# Revit family: Pipefitting_IBP_Conex_MaxiPro_ReducingStraightCoupler_MP5240
name_source: partatom
category: Pipe Fittings
units: mm (PartAtom-declared; Revit-internal decimal feet)

## family parameters
Always vertical = No
Cut with Voids When Loaded = No
OmniClass Number = 23.65.00.00
OmniClass Title = Supply and Distribution of Liquids and Gases
Part Type = Transition
Round Connector Dimension = Use Diameter
Shared = No
Work Plane-Based = No

## types (15) — shared parameters
Angle = 30.00°
Application = Air conditioning & refrigeration
Assembly Code = D20
AssetType = Fixed
BIMObjectName = PipefittingP_IBP_Conex_MaxiPro_ReducingStraightcoupler_MP5240
ClassificationName = Uniclass2015
ClassificationValue = Pr_65_52_63_18
Description = Reducing Straight Coupler
ExpectedServiceLifeYears = 25
FittingType = Reducing Straight Coupler
FluidTemperatureMax = 121 °C
FluidTemperatureMin = -40 °C
IfcExportAs = IfcPipeFitting
IfcExportType = IfcPipeFittingType
Keynote = S
Manufacturer = Conex Banninger
ManufacturerName = IBP
Material = Copper, C12200
MaterialType = Refrigerant Grade Copper, C12200
MaxHydrostaticPressure = 48 bar
NBSDescription = Copper pipeline fittings
NBSObjectName = IBP - Copper pipeline fittings
NBSReference = 90-10-65/315
ORingTemperatureRange = -40°C to 140°C
PipeConnectorType = Press x Press
PressJawCompatability = MaxiPro Jaws supplied by Rothenberger
SealType = HNBR
Shape = Cylindrical
SurfaceFinish = Natural
URL = http://www.conexbanninger.com
WarrantyDescription = Product Guarantee
WarrantyDurationMonths = 60
Weight = 0.00 kg
_BimstoreBibleVersion = 14
_CurrentRevision = 1
_DistributedBy = www.bimmepaus.com.au/
zero-valued in all types: NominalDepth, NominalHeight, NominalLength, _BimSpecGuid

## per-type parameters (varying)
| type | A_OverallLength | Bead_Dia | Bead_Dia1 | DN | DN1 | L2_BeadLocation_Left | L2_BeadLocation_Right | L2_BeadLocation_Right_Formula | Length | Model | ModelNumber | ModelReference | OD | OD1 | ProductCode | Size | TubeStop | TubeStop1 | TubeStop1_Formula | Type Comments |
| MP5240 0030200 3/8" x 1/4" | 44 mm  [stored 0.144357 ft] | 2 mm  [stored 0.00656168 ft] | 2 mm  [stored 0.00656168 ft] | 10 mm  [stored 0.0328084 ft] | 6 mm  [stored 0.019685 ft] | 7 mm  [stored 0.0229659 ft] | 8 mm  [stored 0.0262467 ft] | 37 mm | 44 mm  [stored 0.144357 ft] | MP5240 0030200 | MP5240 0030200 | 3/8" x 1/2" | 12 mm  [stored 0.0393701 ft] | 8 mm  [stored 0.0262467 ft] | MP5240 0030200 | 3/8" x 1/2" | 18 mm  [stored 0.0590551 ft] | 18 mm  [stored 0.0590551 ft] | 26 mm | 3/8" x 1/2" |
| MP5240 0040300 1/2" x 3/8" | 42 mm  [stored 0.137795 ft] | 3 mm  [stored 0.00984252 ft] | 2 mm  [stored 0.00656168 ft] | 13 mm | 10 mm  [stored 0.0328084 ft] | 7 mm  [stored 0.0229659 ft] | 7 mm  [stored 0.0229659 ft] | 35 mm | 42 mm  [stored 0.137795 ft] | MP5240 0040300 | MP5240 0040300 | 1/2" x 3/8" | 16 mm  [stored 0.0524934 ft] | 12 mm  [stored 0.0393701 ft] | MP5240 0040300 | 1/2" x 3/8" | 18 mm  [stored 0.0590551 ft] | 19 mm  [stored 0.062336 ft] | 24 mm  [stored 0.0787402 ft] | 1/2" x 3/8" |
| MP5240 0050300 3/8" x 5/8" | 48 mm  [stored 0.15748 ft] | 3 mm  [stored 0.00984252 ft] | 2 mm  [stored 0.00656168 ft] | 16 mm  [stored 0.0524934 ft] | 10 mm  [stored 0.0328084 ft] | 8 mm  [stored 0.0262467 ft] | 7 mm  [stored 0.0229659 ft] | 41 mm  [stored 0.134514 ft] | 48 mm  [stored 0.15748 ft] | MP5240 0050300 | MP5240 0050300 | 3/8" x 5/8" | 19 mm  [stored 0.062336 ft] | 12 mm  [stored 0.0393701 ft] | MP5240 0050300 | 3/8" x 5/8" | 22 mm  [stored 0.0721785 ft] | 18 mm  [stored 0.0590551 ft] | 30 mm | 3/8" x 5/8" |
| MP5240 0050400 1/2" x 5/8" | 48 mm  [stored 0.15748 ft] | 3 mm  [stored 0.00984252 ft] | 2 mm  [stored 0.00656168 ft] | 16 mm  [stored 0.0524934 ft] | 13 mm | 8 mm  [stored 0.0262467 ft] | 7 mm  [stored 0.0229659 ft] | 41 mm  [stored 0.134514 ft] | 48 mm  [stored 0.15748 ft] | MP5240 0050300 | MP5240 0050300 | 3/8" x 5/8" | 19 mm  [stored 0.062336 ft] | 16 mm  [stored 0.0524934 ft] | MP5240 0050300 | 3/8" x 5/8" | 21 mm  [stored 0.0688976 ft] | 18 mm  [stored 0.0590551 ft] | 30 mm | 3/8" x 5/8" |
| MP5240 0060300 3/8" x 3/4" | 51 mm | 3 mm  [stored 0.00984252 ft] | 2 mm  [stored 0.00656168 ft] | 19 mm  [stored 0.062336 ft] | 10 mm  [stored 0.0328084 ft] | 8 mm  [stored 0.0262467 ft] | 7 mm  [stored 0.0229659 ft] | 44 mm  [stored 0.144357 ft] | 51 mm | MP5240 0060300 | MP5240 0060300 | 3/8" x 3/4" | 22 mm  [stored 0.0721785 ft] | 12 mm  [stored 0.0393701 ft] | MP5240 0060300 | 3/8" x 3/4" | 22 mm  [stored 0.0721785 ft] | 18 mm  [stored 0.0590551 ft] | 33 mm  [stored 0.108268 ft] | 3/8" x 3/4" |
| MP5240 0060400 1/2" x 3/4" | 46 mm  [stored 0.150919 ft] | 3 mm  [stored 0.00984252 ft] | 3 mm  [stored 0.00984252 ft] | 19 mm  [stored 0.062336 ft] | 13 mm | 10 mm  [stored 0.0328084 ft] | 7 mm  [stored 0.0229659 ft] | 39 mm  [stored 0.127953 ft] | 46 mm  [stored 0.150919 ft] | MP5240 0060400 | MP5240 0060400 | 1/2" x 3/4" | 22 mm  [stored 0.0721785 ft] | 15 mm  [stored 0.0492126 ft] | MP5240 0060400 | 1/2" x 3/4" | 22 mm  [stored 0.0721785 ft] | 18 mm  [stored 0.0590551 ft] | 29 mm  [stored 0.0951444 ft] | 1/2" x 3/4" |
| MP5240 0060500 5/8" x 3/4" | 52 mm | 3 mm  [stored 0.00984252 ft] | 3 mm  [stored 0.00984252 ft] | 19 mm  [stored 0.062336 ft] | 16 mm  [stored 0.0524934 ft] | 10 mm  [stored 0.0328084 ft] | 8 mm  [stored 0.0262467 ft] | 44 mm  [stored 0.144357 ft] | 52 mm | MP5240 0060500 | MP5240 0060500 | 5/8" x 3/4" | 22 mm  [stored 0.0721785 ft] | 19 mm  [stored 0.062336 ft] | MP5240 0060500 | 5/8" x 3/4" | 22 mm  [stored 0.0721785 ft] | 21 mm  [stored 0.0688976 ft] | 31 mm | 5/8" x 3/4" |
| MP5240 0070400 1/2" x 7/8" | 52 mm | 3 mm  [stored 0.00984252 ft] | 3 mm  [stored 0.00984252 ft] | 22 mm  [stored 0.0721785 ft] | 13 mm | 10 mm  [stored 0.0328084 ft] | 7 mm  [stored 0.0229659 ft] | 45 mm  [stored 0.147638 ft] | 52 mm | MP5240 0070400 | MP5240 0070400 | 1/2" x 7/8" | 26 mm | 15 mm  [stored 0.0492126 ft] | MP5240 0070400 | 1/2" x 7/8" | 24 mm  [stored 0.0787402 ft] | 18 mm  [stored 0.0590551 ft] | 35 mm | 1/2" x 7/8" |
| MP5240 0070500 5/8" x 7/8" | 52 mm | 3 mm  [stored 0.00984252 ft] | 3 mm  [stored 0.00984252 ft] | 22 mm  [stored 0.0721785 ft] | 16 mm  [stored 0.0524934 ft] | 10 mm  [stored 0.0328084 ft] | 8 mm  [stored 0.0262467 ft] | 44 mm  [stored 0.144357 ft] | 52 mm | MP5240 0070500 | MP5240 0070500 | 5/8" x 7/8" | 26 mm | 19 mm  [stored 0.062336 ft] | MP5240 0070500 | 5/8" x 7/8" | 24 mm  [stored 0.0787402 ft] | 21 mm  [stored 0.0688976 ft] | 31 mm | 5/8" x 7/8" |
| MP5240 0070600 3/4" x 7/8" | 52 mm | 3 mm  [stored 0.00984252 ft] | 3 mm  [stored 0.00984252 ft] | 22 mm  [stored 0.0721785 ft] | 19 mm  [stored 0.062336 ft] | 10 mm  [stored 0.0328084 ft] | 10 mm  [stored 0.0328084 ft] | 42 mm  [stored 0.137795 ft] | 52 mm | MP5240 0070600 | MP5240 0070600 | 3/4" x 7/8" | 26 mm | 22 mm  [stored 0.0721785 ft] | MP5240 0070600 | 3/4" x 7/8" | 24 mm  [stored 0.0787402 ft] | 22 mm  [stored 0.0721785 ft] | 30 mm | 3/4" x 7/8" |
| MP5240 0080600 3/4" x 1" | 51 mm | 3 mm  [stored 0.00984252 ft] | 3 mm  [stored 0.00984252 ft] | 26 mm | 19 mm  [stored 0.062336 ft] | 10 mm  [stored 0.0328084 ft] | 10 mm  [stored 0.0328084 ft] | 41 mm  [stored 0.134514 ft] | 51 mm | MP5240 0080600 | MP5240 0080600 | 3/4" x 1" | 29 mm  [stored 0.0951444 ft] | 22 mm  [stored 0.0721785 ft] | MP5240 0080600 | 3/4" x 1" | 24 mm  [stored 0.0787402 ft] | 22 mm  [stored 0.0721785 ft] | 29 mm  [stored 0.0951444 ft] | 3/4" x 1" |
| MP5240 0090500 5/8" x 1 1/8" | 55 mm  [stored 0.180446 ft] | 3 mm  [stored 0.00984252 ft] | 3 mm  [stored 0.00984252 ft] | 29 mm  [stored 0.0951444 ft] | 16 mm  [stored 0.0524934 ft] | 10 mm  [stored 0.0328084 ft] | 8 mm  [stored 0.0262467 ft] | 47 mm  [stored 0.154199 ft] | 55 mm  [stored 0.180446 ft] | MP5240 0090500 | MP5240 0090500 | 5/8" x 1 1/8" | 32 mm  [stored 0.104987 ft] | 19 mm  [stored 0.062336 ft] | MP5240 0090500 | 5/8" x 1 1/8" | 26 mm | 21 mm  [stored 0.0688976 ft] | 34 mm  [stored 0.111549 ft] | 5/8" x 1 1/8" |
| MP5240 0090600 3/4" x 1 1/8" | 55 mm  [stored 0.180446 ft] | 3 mm  [stored 0.00984252 ft] | 3 mm  [stored 0.00984252 ft] | 29 mm  [stored 0.0951444 ft] | 19 mm  [stored 0.062336 ft] | 10 mm  [stored 0.0328084 ft] | 10 mm  [stored 0.0328084 ft] | 45 mm  [stored 0.147638 ft] | 55 mm  [stored 0.180446 ft] | MP5240 0090600 | MP5240 0090600 | 3/4" x 1 1/8" | 32 mm  [stored 0.104987 ft] | 22 mm  [stored 0.0721785 ft] | MP5240 0090600 | 3/4" x 1 1/8" | 26 mm | 22 mm  [stored 0.0721785 ft] | 33 mm  [stored 0.108268 ft] | 3/4" x 1 1/8" |
| MP5240 0090700 7/8" x 1 1/8" | 58 mm  [stored 0.190289 ft] | 3 mm  [stored 0.00984252 ft] | 3 mm  [stored 0.00984252 ft] | 29 mm  [stored 0.0951444 ft] | 22 mm  [stored 0.0721785 ft] | 10 mm  [stored 0.0328084 ft] | 10 mm  [stored 0.0328084 ft] | 48 mm  [stored 0.15748 ft] | 58 mm  [stored 0.190289 ft] | MP5240 0090700 | MP5240 0090700 | 7/8" x 1 1/8" | 32 mm  [stored 0.104987 ft] | 25 mm  [stored 0.082021 ft] | MP5240 0090700 | 7/8" x 1 1/8" | 26 mm | 24 mm  [stored 0.0787402 ft] | 34 mm  [stored 0.111549 ft] | 7/8" x 1 1/8" |
| MP5240 0090800 1" x 1 1/8" | 58 mm  [stored 0.190289 ft] | 3 mm  [stored 0.00984252 ft] | 3 mm  [stored 0.00984252 ft] | 29 mm  [stored 0.0951444 ft] | 26 mm | 10 mm  [stored 0.0328084 ft] | 10 mm  [stored 0.0328084 ft] | 48 mm  [stored 0.15748 ft] | 58 mm  [stored 0.190289 ft] | MP5240 0090800 | MP5240 0090800 | 1" x 1 1/8" | 32 mm  [stored 0.104987 ft] | 29 mm  [stored 0.0951444 ft] | MP5240 0090800 | 1" x 1 1/8" | 26 mm | 24 mm  [stored 0.0787402 ft] | 35 mm | 1" x 1 1/8" |

note: [stored X ft] marks values corroborated as IEEE doubles in the binary element streams (Revit-internal decimal feet)

## geometry (parser evidence)
native form markers: Blend x2, Sweep x6
no freeform markers — native parametric forms only
